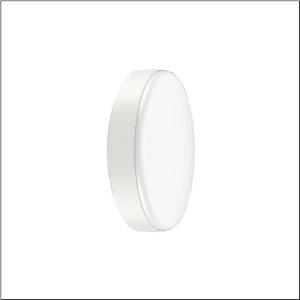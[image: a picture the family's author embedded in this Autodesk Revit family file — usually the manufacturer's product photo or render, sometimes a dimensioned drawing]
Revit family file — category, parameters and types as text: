
# Revit family: rondel_31_51wc10db44a
name_source: partatom
category: Lighting Fixtures
units: mm (PartAtom-declared; Revit-internal decimal feet)

## family parameters
Cut with Voids When Loaded = No
Host = Face
Light Source = No
Part Type = Normal
Room Calculation Point = No
Round Connector Dimension = Use Diameter
Shared = No

## types (1)
- Rondel 31 (1 x LED, 4400 lm, 34 W, 4000K)
    Apparent Load = 34 VA
    CIE Flux Codes = 44 75 94 94 100
    Color Rendering = 80
    Color Temperature = 4000K
    Default Elevation = 1800 mm
    Description = Rondel 31, wall and ceiling luminaire, primary optical cover: cover, of PC, opal, light emission: direct distribution, primary light characteristic: symmetric, installation type: surface-mounted, LED, rated luminous flux: 4.400lm, luminous efficacy: 129lm/W, light colour: 840, colour temperature: 4000K, with terminal, 3-pole, max. 2.5mm², mains connection: 220..240V, AC, 50/60Hz, rated input power: 34W, luminaire housing, of PC, traffic white (RAL 9016), diameter: 480mm, protection rating (complete): IP65, insulation class (complete): insulation class II (safety insulation), certification: CE, impact resistance: IK10, permissible operating ambient temperature: -20..+40°C, permissible storage temperature: -20..+60°C, packaging unit: 1 piece
    Height = 97 mm
    Lamp = 1 x LED
    Lamp Light Flux = 4400 lm
    Lamp Power = 34 W
    Lamp count = 1
    Length = 480 mm
    Luminous efficacy = 129 lm/W
    Manufacturer = Siteco
    ModVariant = No
    Model = 51WC10DB44A
    Mounting Place = Ceiling
    Mounting Type = Surface mounted
    Number of Poles = 1
    OnlyDefault = Yes
    Power Factor = 1
    Product Name = Rondel 31
    Product group = wall and ceiling luminaire
    ProductGroupID = 302
    Protection Class = Protection class II
    Protection Degree = IP 65
    RLX_Detail_Level = 1
    RLX_Emergency_Light_Flux = 0 lm
    RLX_Emergency_Type = 0
    RLX_Emergency_Type_DB = No
    RlxData = <blob elided: 40729 chars, md5=2cd57e72>
    Socket = socket
    Standby Power = 0 W
    System Light Flux = 4400 lm
    System Power = 34 W
    Type Comments = Product without accessories
    Type Image = l_1007188.jpg
    URL = http://relux.com
    VarID = ---
    Voltage = 0 V
    Weight = 0.00 kg
    Width = 0 mm  [stored 0 ft]

note: [stored X ft] marks values corroborated as IEEE doubles in the binary element streams (Revit-internal decimal feet)

## geometry (parser evidence)
native form markers: Blend x4, Sweep x11
no freeform markers — native parametric forms only
